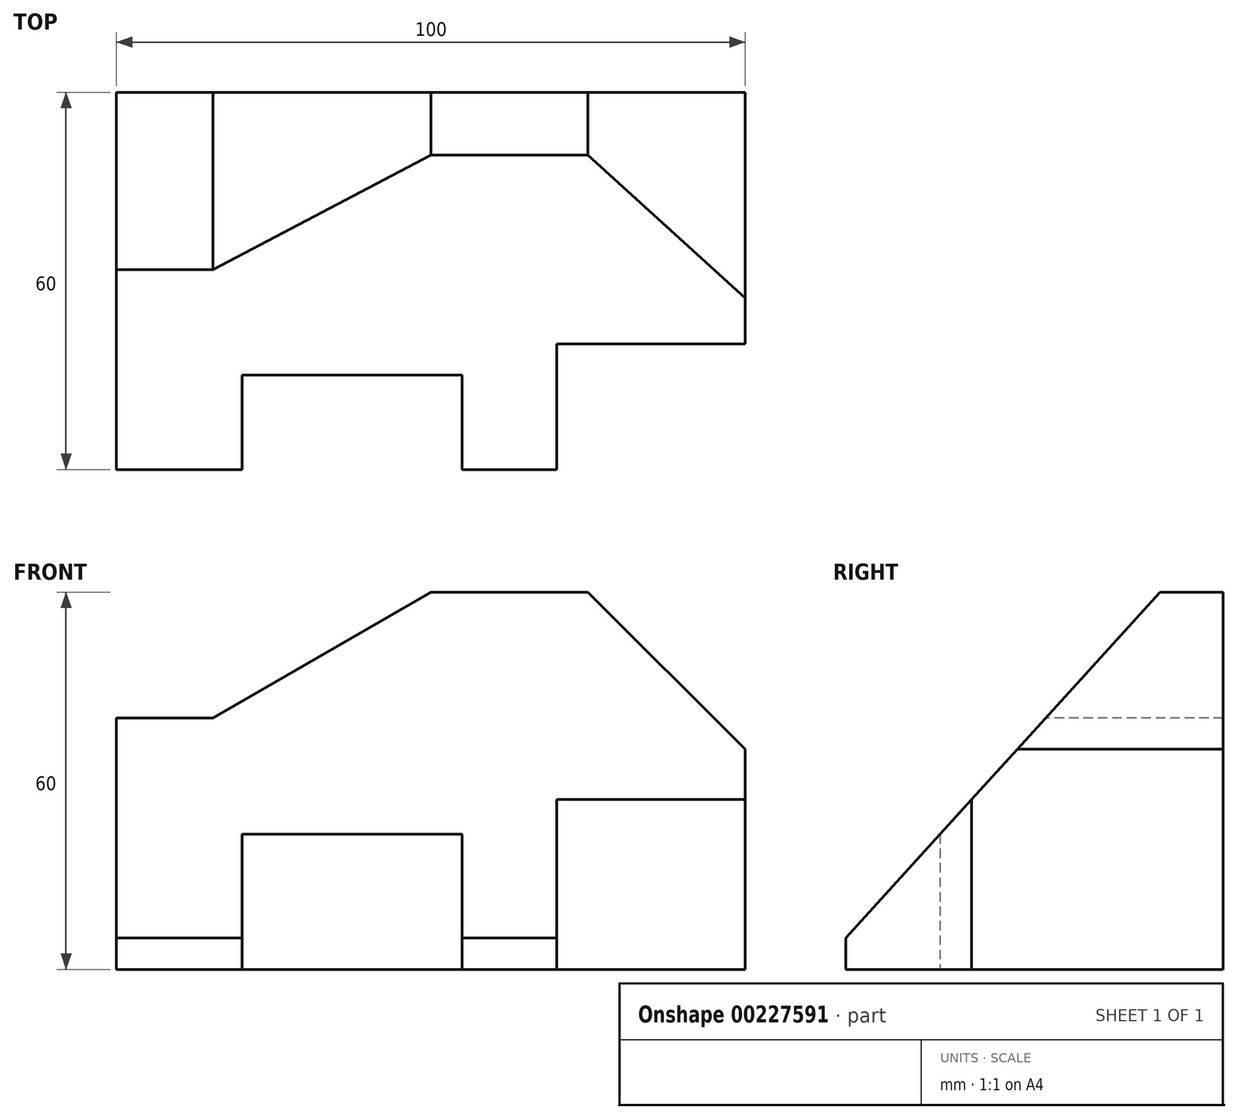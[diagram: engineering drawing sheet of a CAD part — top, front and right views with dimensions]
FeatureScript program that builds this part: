
annotation { "Feature Type Name" : "Feature", "Feature Type Description" : "" }
export const myFeature = defineFeature(function(context is Context, id is Id, definition is map)
    precondition{}
    {
        {
            var Q0;
            Q0=qCreatedBy(makeId("Top.planeOp"),FACE);
            var sketch = newSketch(context, id + "F0", { "sketchPlane" : qUnion([Q0])});
            skLineSegment(sketch, "E0", {"start": v(0, 60) * mm, "end": v(0, 0) * mm});
            skLineSegment(sketch, "E1", {"start": v(0, 0) * mm, "end": v(20, 0) * mm});
            skLineSegment(sketch, "E2", {"start": v(20, 0) * mm, "end": v(20, 15) * mm});
            skLineSegment(sketch, "E3", {"start": v(20, 15) * mm, "end": v(55, 15) * mm});
            skLineSegment(sketch, "E4", {"start": v(55, 15) * mm, "end": v(55, 0) * mm});
            skLineSegment(sketch, "E5", {"start": v(55, 0) * mm, "end": v(70, 0) * mm});
            skLineSegment(sketch, "E6", {"start": v(70, 0) * mm, "end": v(70, 20) * mm});
            skLineSegment(sketch, "E7", {"start": v(70, 20) * mm, "end": v(100, 20) * mm});
            skLineSegment(sketch, "E8", {"start": v(100, 20) * mm, "end": v(100, 60) * mm});
            skLineSegment(sketch, "E9", {"start": v(100, 60) * mm, "end": v(0, 60) * mm});
            skSolve(sketch);
        }
        {
            var Q0;
            Q0=makeQuery(id+"F0.imprint","IMPRINT",FACE,{"disambiguationData":[TD([[makeQuery(id+"F0.imprint","IMPRINT",EDGE,{"derivedFrom":sQuery(id+"F0.wireOp",EDGE,"E0")}),1.0]])]});
            extrude(context, id + "F1", {"entities" : qUnion([Q0]), "depth" : 60 * mm});
        }
        {
            var Q0;
            Q0=qCreatedBy(makeId("Front.planeOp"),FACE);
            var sketch = newSketch(context, id + "F2", { "sketchPlane" : qUnion([Q0])});
            skLineSegment(sketch, "E10.0.0", {"start": v(0, 0) * mm, "end": v(20, 0) * mm, "construction": true});
            skLineSegment(sketch, "E10.0.1", {"start": v(20, 0) * mm, "end": v(20, 60) * mm, "construction": true});
            skLineSegment(sketch, "E10.0.2", {"start": v(20, 60) * mm, "end": v(0, 60) * mm, "construction": true});
            skLineSegment(sketch, "E10.0.3", {"start": v(0, 60) * mm, "end": v(0, 0) * mm, "construction": true});
            skLineSegment(sketch, "E11.0.0", {"start": v(20, 0) * mm, "end": v(55, 0) * mm, "construction": true});
            skLineSegment(sketch, "E11.0.1", {"start": v(55, 0) * mm, "end": v(55, 60) * mm, "construction": true});
            skLineSegment(sketch, "E11.0.2", {"start": v(55, 60) * mm, "end": v(20, 60) * mm, "construction": true});
            skLineSegment(sketch, "E11.0.3", {"start": v(20, 60) * mm, "end": v(20, 0) * mm, "construction": true});
            skLineSegment(sketch, "E12.0.0", {"start": v(55, 0) * mm, "end": v(70, 0) * mm, "construction": true});
            skLineSegment(sketch, "E12.0.1", {"start": v(70, 0) * mm, "end": v(70, 60) * mm, "construction": true});
            skLineSegment(sketch, "E12.0.2", {"start": v(70, 60) * mm, "end": v(55, 60) * mm, "construction": true});
            skLineSegment(sketch, "E12.0.3", {"start": v(55, 60) * mm, "end": v(55, 0) * mm, "construction": true});
            skLineSegment(sketch, "E13.0.0", {"start": v(70, 0) * mm, "end": v(100, 0) * mm, "construction": true});
            skLineSegment(sketch, "E13.0.1", {"start": v(100, 0) * mm, "end": v(100, 60) * mm, "construction": true});
            skLineSegment(sketch, "E13.0.2", {"start": v(100, 60) * mm, "end": v(70, 60) * mm, "construction": true});
            skLineSegment(sketch, "E13.0.3", {"start": v(70, 60) * mm, "end": v(70, 0) * mm, "construction": true});
            skLineSegment(sketch, "E14", {"start": v(50, 60) * mm, "end": v(15.36, 40) * mm});
            skLineSegment(sketch, "E15", {"start": v(15.36, 40) * mm, "end": v(0, 40) * mm});
            skLineSegment(sketch, "E16", {"start": v(0, 40) * mm, "end": v(0, 60) * mm});
            skLineSegment(sketch, "E17", {"start": v(0, 60) * mm, "end": v(50, 60) * mm});
            skLineSegment(sketch, "E18", {"start": v(75, 60) * mm, "end": v(100, 35) * mm});
            skLineSegment(sketch, "E19", {"start": v(100, 35) * mm, "end": v(100, 60) * mm});
            skLineSegment(sketch, "E20", {"start": v(100, 60) * mm, "end": v(75, 60) * mm});
            skSolve(sketch);
        }
        {
            var Q0;
            Q0=makeQuery(id+"F2.imprint","IMPRINT",FACE,{"disambiguationData":[TD([[makeQuery(id+"F2.imprint","IMPRINT",EDGE,{"derivedFrom":sQuery(id+"F2.wireOp",EDGE,"E14")}),-1.0]])]});
            var Q1;
            Q1=makeQuery(id+"F2.imprint","IMPRINT",FACE,{"disambiguationData":[TD([[makeQuery(id+"F2.imprint","IMPRINT",EDGE,{"derivedFrom":sQuery(id+"F2.wireOp",EDGE,"E18")}),1.0]])]});
            var Q2;
            Q2=makeQuery(id+"F1.opExtrude","SWEPT_FACE",FACE,{"disambiguationData":[OSD([sQuery(id+"F0.wireOp",EDGE,"E3")])]});
            extrude(context, id + "F3", {"entities" : qUnion([Q0, Q1]), "operationType" : NewBodyOperationType.REMOVE, "endBound" : BoundingType.THROUGH_ALL, "oppositeDirection" : true, "endBoundEntityFace" : qUnion([Q2]), "depth" : 25 * mm});
        }
        {
            var Q0;
            Q0=qCreatedBy(makeId("Right.planeOp"),FACE);
            var sketch = newSketch(context, id + "F4", { "sketchPlane" : qUnion([Q0])});
            skLineSegment(sketch, "E21.0.0", {"start": v(60, 60) * mm, "end": v(20, 60) * mm, "construction": true});
            skLineSegment(sketch, "E21.0.1", {"start": v(20, 60) * mm, "end": v(20, 35) * mm, "construction": true});
            skLineSegment(sketch, "E21.0.2", {"start": v(20, 35) * mm, "end": v(60, 35) * mm, "construction": true});
            skLineSegment(sketch, "E21.0.3", {"start": v(60, 35) * mm, "end": v(60, 60) * mm, "construction": true});
            skLineSegment(sketch, "E22.0.0", {"start": v(0, 0) * mm, "end": v(20, 0) * mm, "construction": true});
            skLineSegment(sketch, "E22.0.1", {"start": v(20, 0) * mm, "end": v(20, 60) * mm, "construction": true});
            skLineSegment(sketch, "E22.0.2", {"start": v(20, 60) * mm, "end": v(0, 60) * mm, "construction": true});
            skLineSegment(sketch, "E22.0.3", {"start": v(0, 60) * mm, "end": v(0, 0) * mm, "construction": true});
            skLineSegment(sketch, "E23.0.0", {"start": v(60, 0) * mm, "end": v(60, 35) * mm, "construction": true});
            skLineSegment(sketch, "E23.0.1", {"start": v(60, 35) * mm, "end": v(20, 35) * mm, "construction": true});
            skLineSegment(sketch, "E23.0.2", {"start": v(20, 35) * mm, "end": v(20, 0) * mm, "construction": true});
            skLineSegment(sketch, "E23.0.3", {"start": v(20, 0) * mm, "end": v(60, 0) * mm, "construction": true});
            skLineSegment(sketch, "E24", {"start": v(50, 60) * mm, "end": v(0, 5) * mm});
            skLineSegment(sketch, "E25", {"start": v(0, 5) * mm, "end": v(0, 60) * mm});
            skLineSegment(sketch, "E26", {"start": v(50, 60) * mm, "end": v(0, 60) * mm});
            skSolve(sketch);
        }
        {
            var Q0;
            Q0=makeQuery(id+"F4.imprint","IMPRINT",FACE,{"disambiguationData":[TD([[makeQuery(id+"F4.imprint","IMPRINT",EDGE,{"derivedFrom":sQuery(id+"F4.wireOp",EDGE,"E24")}),-1.0]])]});
            extrude(context, id + "F5", {"entities" : qUnion([Q0]), "operationType" : NewBodyOperationType.REMOVE, "endBound" : BoundingType.THROUGH_ALL, "depth" : 128 * mm});
        }
    });
